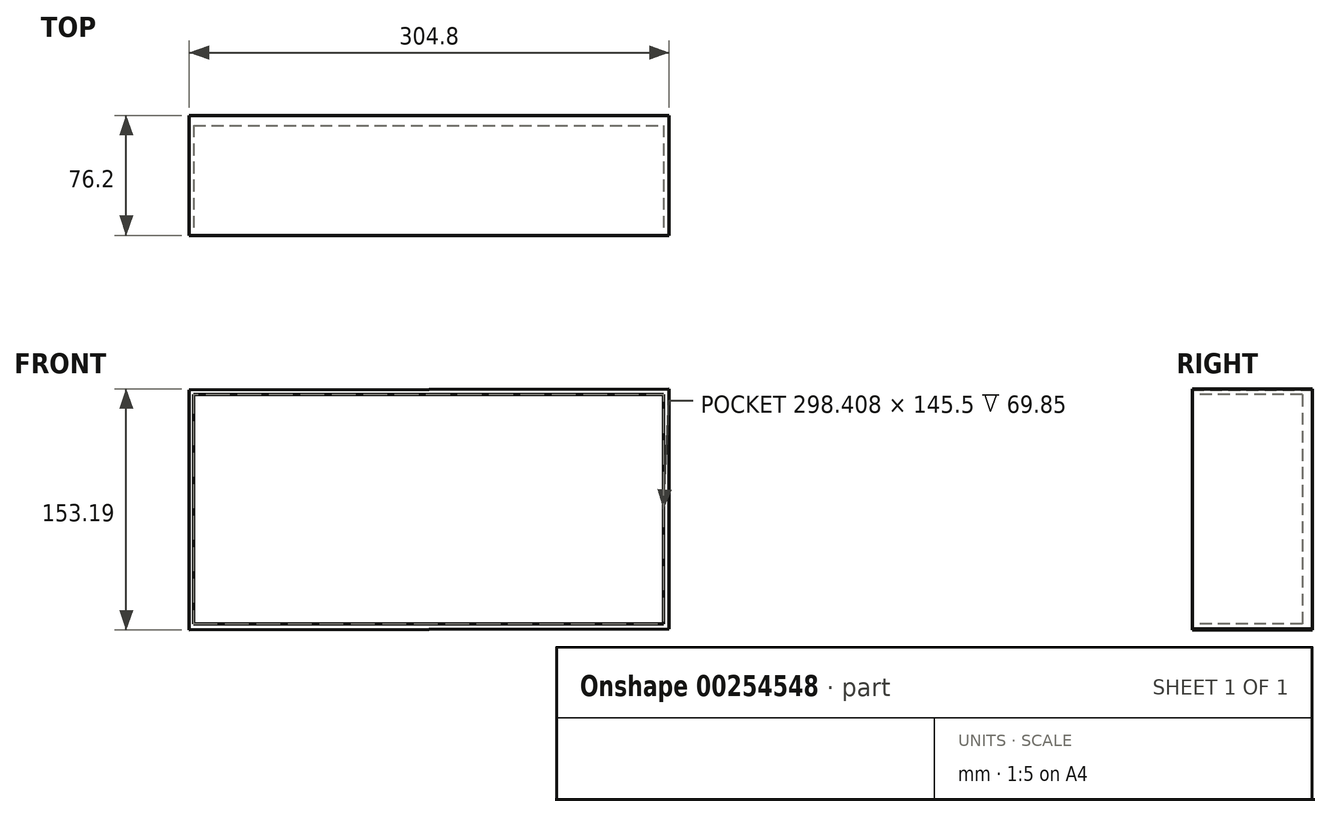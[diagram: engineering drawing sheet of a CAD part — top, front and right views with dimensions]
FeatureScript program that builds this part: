
annotation { "Feature Type Name" : "Feature", "Feature Type Description" : "" }
export const myFeature = defineFeature(function(context is Context, id is Id, definition is map)
    precondition{}
    {
        {
            var Q0;
            Q0=qCreatedBy(makeId("Front.planeOp"),FACE);
            var sketch = newSketch(context, id + "F0", { "sketchPlane" : qUnion([Q0])});
            skLineSegment(sketch, "E0", {"start": v(-86.64, 74.69) * mm, "end": v(-86.64, -77.71) * mm});
            skLineSegment(sketch, "E1", {"start": v(218.16, 75.48) * mm, "end": v(218.16, -76.92) * mm});
            skLineSegment(sketch, "E2", {"start": v(-86.64, 74.69) * mm, "end": v(218.16, 75.48) * mm});
            skLineSegment(sketch, "E3", {"start": v(-86.64, -77.71) * mm, "end": v(218.16, -76.92) * mm});
            skSolve(sketch);
        }
        {
            var Q0;
            Q0=makeQuery(id+"F0.imprint","IMPRINT",FACE,{"disambiguationData":[TD([[makeQuery(id+"F0.imprint","IMPRINT",EDGE,{"derivedFrom":sQuery(id+"F0.wireOp",EDGE,"E0")}),1.0]])]});
            extrude(context, id + "F1", {"entities" : qUnion([Q0]), "depth" : 76.2 * mm});
        }
        {
            var Q0;
            Q0=makeQuery(id+"F1.opExtrude","CAP_FACE",FACE,{"disambiguationData":[OSD([sQuery(id+"F0.wireOp",EDGE,"E0"),sQuery(id+"F0.wireOp",EDGE,"E1"),sQuery(id+"F0.wireOp",EDGE,"E2"),sQuery(id+"F0.wireOp",EDGE,"E3")])],"isStart":false});
            var sketch = newSketch(context, id + "F2", { "sketchPlane" : qUnion([Q0])});
            skLineSegment(sketch, "E4.bottom", {"start": v(-83.9, 71.85) * mm, "end": v(214.52, 71.85) * mm});
            skLineSegment(sketch, "E4.top", {"start": v(-83.9, -73.65) * mm, "end": v(214.52, -73.65) * mm});
            skLineSegment(sketch, "E4.left", {"start": v(-83.9, 71.85) * mm, "end": v(-83.9, -73.65) * mm});
            skLineSegment(sketch, "E4.right", {"start": v(214.52, 71.85) * mm, "end": v(214.52, -73.65) * mm});
            skSolve(sketch);
        }
        {
            var Q0;
            Q0 = qSketchRegion(id + "F2", true);
            extrude(context, id + "F3", {"entities" : qUnion([Q0]), "operationType" : NewBodyOperationType.REMOVE, "oppositeDirection" : true, "depth" : 69.85 * mm});
        }
    });
